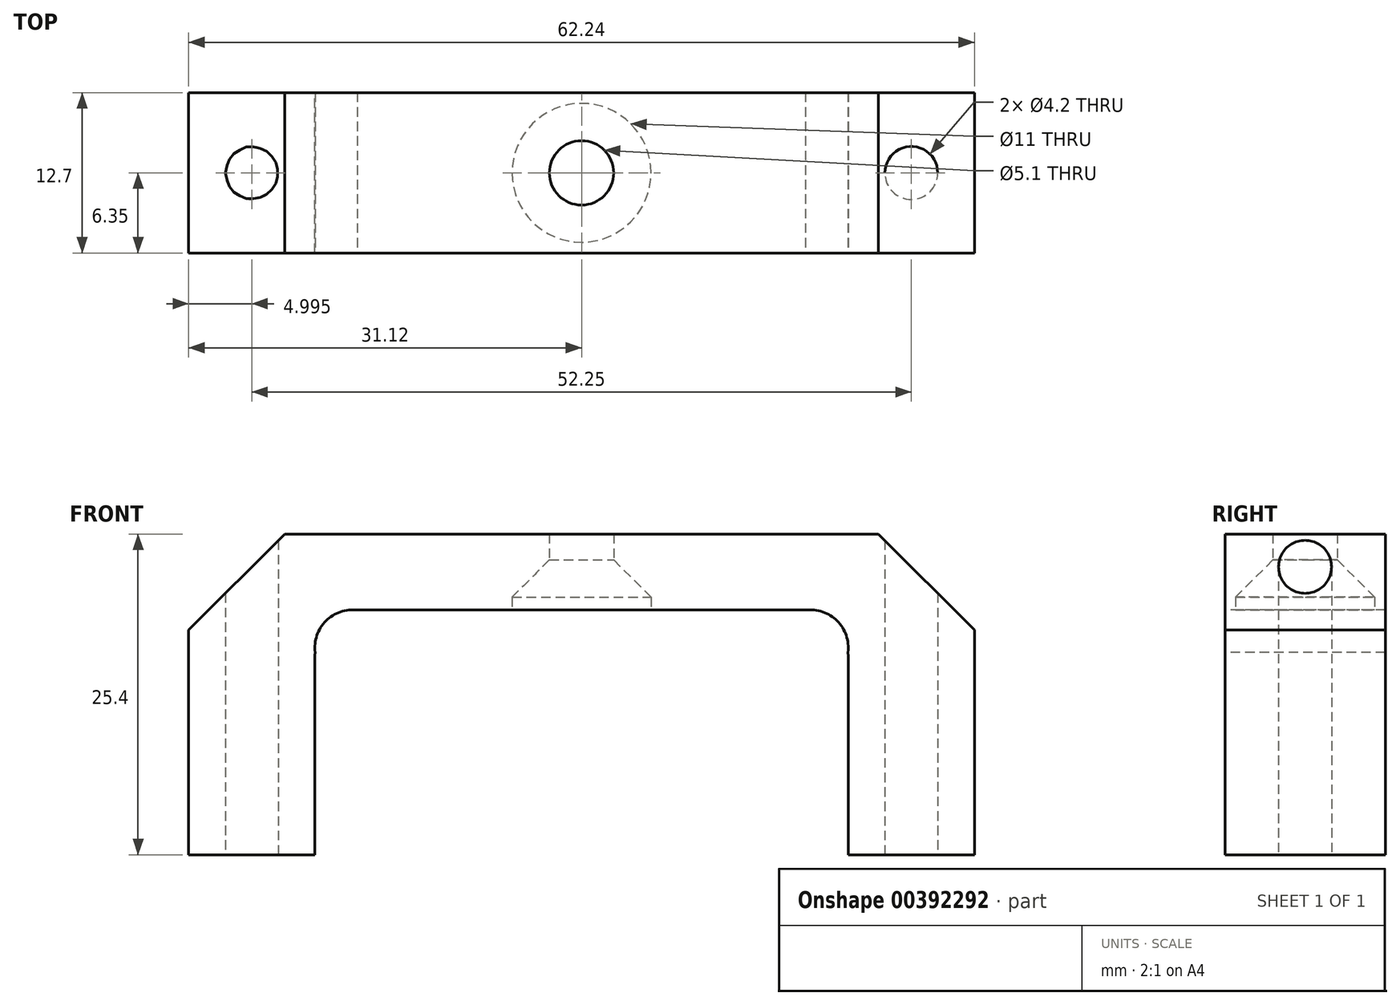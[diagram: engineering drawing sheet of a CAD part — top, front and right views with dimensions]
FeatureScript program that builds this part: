
annotation { "Feature Type Name" : "Feature", "Feature Type Description" : "" }
export const myFeature = defineFeature(function(context is Context, id is Id, definition is map)
    precondition{}
    {
        {
            var Q0;
            Q0=qCreatedBy(makeId("Front.planeOp"),FACE);
            var sketch = newSketch(context, id + "F0", { "sketchPlane" : qUnion([Q0])});
            skLineSegment(sketch, "E0", {"start": v(-31.12, 0) * mm, "end": v(-21.12, 0) * mm});
            skLineSegment(sketch, "E1", {"start": v(-21.12, 0) * mm, "end": v(-21.12, 11.8) * mm});
            skLineSegment(sketch, "E2", {"start": v(-21.13, 11.8) * mm, "end": v(-13.53, 19.4) * mm});
            skLineSegment(sketch, "E3", {"start": v(-13.53, 19.4) * mm, "end": v(13.53, 19.4) * mm});
            skLineSegment(sketch, "E4", {"start": v(13.53, 19.4) * mm, "end": v(21.13, 11.8) * mm});
            skLineSegment(sketch, "E5", {"start": v(21.13, 11.8) * mm, "end": v(21.13, 0) * mm});
            skLineSegment(sketch, "E6", {"start": v(21.13, 0) * mm, "end": v(31.13, 0) * mm});
            skLineSegment(sketch, "E7", {"start": v(-31.12, 17.8) * mm, "end": v(-23.52, 25.4) * mm});
            skLineSegment(sketch, "E8", {"start": v(23.53, 25.4) * mm, "end": v(31.13, 17.8) * mm});
            skLineSegment(sketch, "E9", {"start": v(-23.52, 25.4) * mm, "end": v(23.53, 25.4) * mm});
            skLineSegment(sketch, "E10", {"start": v(-31.12, 17.8) * mm, "end": v(-31.13, 0) * mm});
            skLineSegment(sketch, "E11", {"start": v(31.13, 17.8) * mm, "end": v(31.13, 0) * mm});
            skSolve(sketch);
        }
        {
            var Q0;
            Q0=makeQuery(id+"F0.imprint","IMPRINT",FACE,{"disambiguationData":[TD([[makeQuery(id+"F0.imprint","IMPRINT",EDGE,{"derivedFrom":sQuery(id+"F0.wireOp",EDGE,"E0")}),1.0]])]});
            extrude(context, id + "F1", {"entities" : qUnion([Q0]), "endBound" : BoundingType.SYMMETRIC, "depth" : 12.7 * mm});
        }
        {
            var Q0;
            Q0=makeQuery(id+"F1.opExtrude","SWEPT_FACE",FACE,{"disambiguationData":[OSD([sQuery(id+"F0.wireOp",EDGE,"E3")])]});
            var sketch = newSketch(context, id + "F2", { "sketchPlane" : qUnion([Q0])});
            skPoint(sketch, "E12", {"position": v(0, 0) * mm});
            skCircle(sketch, "E13", {"center": v(0, 0) * mm, "radius": 5.5 * mm});
            skSolve(sketch);
        }
        {
            var Q0;
            Q0=qCreatedBy(makeId("Top.planeOp"),FACE);
            var sketch = newSketch(context, id + "F3", { "sketchPlane" : qUnion([Q0])});
            skPoint(sketch, "E14", {"position": v(-26.12, 0) * mm});
            skPoint(sketch, "E15", {"position": v(26.13, 0) * mm});
            skSolve(sketch);
        }
        {
            var Q0;
            Q0=sQuery(id+"F3.wireOp",VERTEX,"E14");
            var Q1;
            Q1=sQuery(id+"F3.wireOp",VERTEX,"E15");
            var Q2;
            Q2=makeQuery(id+"F1.opExtrude","SWEPT_BODY",BODY,{"disambiguationData":[OSD([sQuery(id+"F0.wireOp",EDGE,"E0"),sQuery(id+"F0.wireOp",EDGE,"E1"),sQuery(id+"F0.wireOp",EDGE,"E2"),sQuery(id+"F0.wireOp",EDGE,"E3"),sQuery(id+"F0.wireOp",EDGE,"E4"),sQuery(id+"F0.wireOp",EDGE,"E5"),sQuery(id+"F0.wireOp",EDGE,"E6"),sQuery(id+"F0.wireOp",EDGE,"E7"),sQuery(id+"F0.wireOp",EDGE,"E8"),sQuery(id+"F0.wireOp",EDGE,"E9"),sQuery(id+"F0.wireOp",EDGE,"E10"),sQuery(id+"F0.wireOp",EDGE,"E11")])]});
            hole(context, id + "F4", {"style" : HoleStyle.SIMPLE, "endStyle" : HoleEndStyle.THROUGH, "oppositeDirection" : true, "standardTappedOrClearance" : lookupTablePath({ "standard" : "ISO", "engagement" : "75%", "pitch" : "0.8 mm", "size" : "M5", "type" : "Tapped" }), "standardBlindInLast" : lookupTablePath({ "standard" : "ISO", "engagement" : "75%", "pitch" : "0.8 mm", "size" : "M5", "type" : "Tapped" }), "holeDiameter" : 4.2 * mm, "showTappedDepth" : true, "isTappedThrough" : true, "tappedDepth" : 12 * mm, "tapClearance" : 3, "startFromSketch" : true, "locations" : qUnion([Q0, Q1]), "scope" : qUnion([Q2]), "majorDiameter" : 5 * mm});
        }
        {
            var Q0;
            Q0=makeQuery(id+"F1.opExtrude","CAP_FACE",FACE,{"disambiguationData":[OSD([sQuery(id+"F0.wireOp",EDGE,"E0"),sQuery(id+"F0.wireOp",EDGE,"E1"),sQuery(id+"F0.wireOp",EDGE,"E2"),sQuery(id+"F0.wireOp",EDGE,"E3"),sQuery(id+"F0.wireOp",EDGE,"E4"),sQuery(id+"F0.wireOp",EDGE,"E5"),sQuery(id+"F0.wireOp",EDGE,"E6"),sQuery(id+"F0.wireOp",EDGE,"E7"),sQuery(id+"F0.wireOp",EDGE,"E8"),sQuery(id+"F0.wireOp",EDGE,"E9"),sQuery(id+"F0.wireOp",EDGE,"E10"),sQuery(id+"F0.wireOp",EDGE,"E11")])],"isStart":false});
            var sketch = newSketch(context, id + "F5", { "sketchPlane" : qUnion([Q0])});
            skCircle(sketch, "E16", {"center": v(-17.33, 15.6) * mm, "radius": 3.8 * mm});
            skCircle(sketch, "E17", {"center": v(17.33, 15.6) * mm, "radius": 3.8 * mm});
            skLineSegment(sketch, "E18", {"start": v(-21.12, 11.8) * mm, "end": v(-21.12, 15.6) * mm});
            skLineSegment(sketch, "E19", {"start": v(-21.12, 15.6) * mm, "end": v(-21.41, 16.02) * mm});
            skLineSegment(sketch, "E20", {"start": v(-13.53, 19.4) * mm, "end": v(-17.33, 19.4) * mm});
            skLineSegment(sketch, "E21", {"start": v(13.53, 19.4) * mm, "end": v(17.32, 19.4) * mm});
            skLineSegment(sketch, "E22", {"start": v(21.13, 11.8) * mm, "end": v(21.13, 15.6) * mm});
            skLineSegment(sketch, "E23", {"start": v(21.13, 15.6) * mm, "end": v(21.4, 15.27) * mm});
            skSolve(sketch);
        }
        {
            var Q0;
            {var subQ0=sQuery(id+"F5.wireOp",EDGE,"E16");var subQ1=makeQuery(id+"F5.imprint","INTERSECT",VERTEX,{"derivedFrom":[subQ0,sQuery(id+"F5.wireOp",EDGE,"E20")]});Q0=makeQuery(id+"F5.imprint","IMPRINT",FACE,{"disambiguationData":[TD([[makeQuery(id+"F5.imprint","IMPRINT",EDGE,{"disambiguationData":[TD([[subQ1,1.0]])],"derivedFrom":subQ0}),1.0]])]});}
            var Q1;
            {var subQ0=sQuery(id+"F5.wireOp",EDGE,"E20");Q1=makeQuery(id+"F5.imprint","IMPRINT",FACE,{"disambiguationData":[TD([[makeQuery(id+"F5.imprint","IMPRINT",EDGE,{"derivedFrom":subQ0}),1.0]])]});}
            var Q2;
            {var subQ0=sQuery(id+"F5.wireOp",EDGE,"E18");Q2=makeQuery(id+"F5.imprint","IMPRINT",FACE,{"disambiguationData":[TD([[makeQuery(id+"F5.imprint","IMPRINT",EDGE,{"derivedFrom":subQ0}),-1.0]])]});}
            var Q3;
            {var subQ0=sQuery(id+"F5.wireOp",EDGE,"E17");var subQ1=makeQuery(id+"F5.imprint","INTERSECT",VERTEX,{"derivedFrom":[subQ0,sQuery(id+"F5.wireOp",EDGE,"E21")]});Q3=makeQuery(id+"F5.imprint","IMPRINT",FACE,{"disambiguationData":[TD([[makeQuery(id+"F5.imprint","IMPRINT",EDGE,{"disambiguationData":[TD([[subQ1,1.0]])],"derivedFrom":subQ0}),1.0]])]});}
            var Q4;
            {var subQ0=sQuery(id+"F5.wireOp",EDGE,"E21");Q4=makeQuery(id+"F5.imprint","IMPRINT",FACE,{"disambiguationData":[TD([[makeQuery(id+"F5.imprint","IMPRINT",EDGE,{"derivedFrom":subQ0}),-1.0]])]});}
            var Q5;
            {var subQ0=sQuery(id+"F5.wireOp",EDGE,"E22");Q5=makeQuery(id+"F5.imprint","IMPRINT",FACE,{"disambiguationData":[TD([[makeQuery(id+"F5.imprint","IMPRINT",EDGE,{"derivedFrom":subQ0}),1.0]])]});}
            extrude(context, id + "F6", {"entities" : qUnion([Q0, Q1, Q2, Q3, Q4, Q5]), "operationType" : NewBodyOperationType.REMOVE, "endBound" : BoundingType.THROUGH_ALL, "oppositeDirection" : true, "depth" : 25 * mm});
        }
        {
            var Q0;
            Q0=makeQuery(id+"F1.opExtrude","CAP_FACE",FACE,{"disambiguationData":[OSD([sQuery(id+"F0.wireOp",EDGE,"E0"),sQuery(id+"F0.wireOp",EDGE,"E1"),sQuery(id+"F0.wireOp",EDGE,"E2"),sQuery(id+"F0.wireOp",EDGE,"E3"),sQuery(id+"F0.wireOp",EDGE,"E4"),sQuery(id+"F0.wireOp",EDGE,"E5"),sQuery(id+"F0.wireOp",EDGE,"E6"),sQuery(id+"F0.wireOp",EDGE,"E7"),sQuery(id+"F0.wireOp",EDGE,"E8"),sQuery(id+"F0.wireOp",EDGE,"E9"),sQuery(id+"F0.wireOp",EDGE,"E10"),sQuery(id+"F0.wireOp",EDGE,"E11")])],"isStart":false});
            var sketch = newSketch(context, id + "F7", { "sketchPlane" : qUnion([Q0])});
            skCircle(sketch, "E24", {"center": v(-18.13, 16.4) * mm, "radius": 3 * mm});
            skCircle(sketch, "E25", {"center": v(18.13, 16.4) * mm, "radius": 3 * mm});
            skSolve(sketch);
        }
        {
            var Q0;
            {var subQ0=sQuery(id+"F7.wireOp",EDGE,"E24");var subQ1=makeQuery(id+"F6.boolean.opBoolean","COPY",EDGE,{"derivedFrom":makeQuery(id+"F6.opExtrude","CAP_EDGE",EDGE,{"disambiguationData":[OSD([sQuery(id+"F5.wireOp",EDGE,"E16")])],"isStart":true})});var subQ2=makeQuery(id+"F7.imprint","INTERSECT",VERTEX,{"disambiguationData":[OD(0.0)],"derivedFrom":[subQ1,subQ0]});Q0=makeQuery(id+"F7.imprint","IMPRINT",FACE,{"disambiguationData":[TD([[makeQuery(id+"F7.imprint","IMPRINT",EDGE,{"disambiguationData":[TD([[subQ2,1.0]])],"derivedFrom":subQ0}),1.0]])]});}
            var Q1;
            {var subQ0=sQuery(id+"F7.wireOp",EDGE,"E25");var subQ1=makeQuery(id+"F6.boolean.opBoolean","COPY",EDGE,{"derivedFrom":makeQuery(id+"F6.opExtrude","CAP_EDGE",EDGE,{"disambiguationData":[OSD([sQuery(id+"F5.wireOp",EDGE,"E17")])],"isStart":true})});var subQ2=makeQuery(id+"F7.imprint","INTERSECT",VERTEX,{"disambiguationData":[OD(0.0)],"derivedFrom":[subQ1,subQ0]});Q1=makeQuery(id+"F7.imprint","IMPRINT",FACE,{"disambiguationData":[TD([[makeQuery(id+"F7.imprint","IMPRINT",EDGE,{"disambiguationData":[TD([[subQ2,1.0]])],"derivedFrom":subQ0}),1.0]])]});}
            extrude(context, id + "F8", {"entities" : qUnion([Q0, Q1]), "operationType" : NewBodyOperationType.REMOVE, "endBound" : BoundingType.THROUGH_ALL, "oppositeDirection" : true, "depth" : 25 * mm});
        }
        {
            var Q0;
            Q0 = qSketchRegion(id + "F2", true);
            extrude(context, id + "F9", {"entities" : qUnion([Q0]), "operationType" : NewBodyOperationType.REMOVE, "oppositeDirection" : true, "depth" : 1 * mm});
        }
        {
            var Q0;
            Q0=makeQuery(id+"F9.boolean.opBoolean","COPY",FACE,{"derivedFrom":makeQuery(id+"F9.opExtrude","CAP_FACE",FACE,{"disambiguationData":[OSD([sQuery(id+"F2.wireOp",EDGE,"E13")])],"isStart":false})});
            var sketch = newSketch(context, id + "F10", { "sketchPlane" : qUnion([Q0])});
            skPoint(sketch, "E26", {"position": v(0, 0) * mm});
            skSolve(sketch);
        }
        {
            var Q0;
            Q0=sQuery(id+"F10.wireOp",VERTEX,"E26");
            var Q1;
            Q1=makeQuery(id+"F1.opExtrude","SWEPT_BODY",BODY,{"disambiguationData":[OSD([sQuery(id+"F0.wireOp",EDGE,"E0"),sQuery(id+"F0.wireOp",EDGE,"E1"),sQuery(id+"F0.wireOp",EDGE,"E2"),sQuery(id+"F0.wireOp",EDGE,"E3"),sQuery(id+"F0.wireOp",EDGE,"E4"),sQuery(id+"F0.wireOp",EDGE,"E5"),sQuery(id+"F0.wireOp",EDGE,"E6"),sQuery(id+"F0.wireOp",EDGE,"E7"),sQuery(id+"F0.wireOp",EDGE,"E8"),sQuery(id+"F0.wireOp",EDGE,"E9"),sQuery(id+"F0.wireOp",EDGE,"E10"),sQuery(id+"F0.wireOp",EDGE,"E11")])]});
            hole(context, id + "F11", {"style" : HoleStyle.C_SINK, "endStyle" : HoleEndStyle.THROUGH, "holeDiameter" : 5.1 * mm, "cSinkDiameter" : 11 * mm, "cSinkAngle" : 90 * degree, "isTappedThrough" : true, "tappedDepth" : 12 * mm, "tapClearance" : 3, "startFromSketch" : true, "locations" : qUnion([Q0]), "scope" : qUnion([Q1])});
        }
    });
